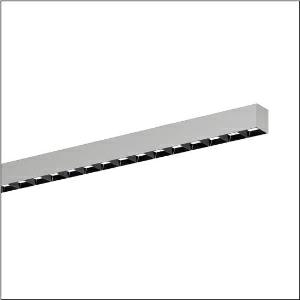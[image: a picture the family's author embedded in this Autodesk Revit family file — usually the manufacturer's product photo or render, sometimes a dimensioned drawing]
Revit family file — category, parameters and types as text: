
# Revit family: silica_r__21_51mx24tctas_d744
name_source: partatom
category: Lighting Fixtures
units: mm (PartAtom-declared; Revit-internal decimal feet)

## family parameters
Cut with Voids When Loaded = No
Host = Face
Light Source = No
Part Type = Normal
Room Calculation Point = No
Round Connector Dimension = Use Diameter
Shared = No

## types (1)
- --- (1 x LED, 8200 lm, 81.1 W, 6500K)
    Apparent Load = 81 VA
    CIE Flux Codes = 74 94 99 100 100
    Color Rendering = 80
    Color Temperature = 6500K
    Default Elevation = 1800 mm
    Description = Silica® 21, office luminaire, primary light control with darklight reflector, of PMMA, black, light emission: direct distribution, primary light characteristic: asymmetric, installation type: surface-mounted, LED, rated luminous flux: 8.200lm, luminous efficacy: 96lm/W, light colour: 8tw, colour temperature: 2700..6500K, control gear: ECG DALI, with terminal, 3+2-pole, max. 2.5mm², mains connection: 220..240V, AC, 50/60Hz, rated input power: 85.2W, luminaire housing, of aluminium, metallic grey (RAL 9006), length: 3.004mm, width: 53mm, height: 53mm, protection rating (complete): IP20, insulation class (complete): insulation class I (protective earthing), certification: CE, permissible operating ambient temperature: 0..+35°C, standard: EN 50419, packaging unit: 1 piece
    Height = 0 mm  [stored 0 ft]
    Lamp = 1 x LED
    Lamp Light Flux = 8200 lm
    Lamp Power = 81.1 W
    Lamp count = 1
    Length = 3004 mm
    Luminous efficacy = 101 lm/W
    Manufacturer = Siteco
    ModVariant = No
    Model = 51MX24TCTAS
    Mounting Place = Ceiling
    Mounting Type = Recessed
    Number of Poles = 1
    OnlyDefault = Yes
    Power Factor = 1
    Product Name = Silica® 21
    Product group = office luminaire | ceiling recessed
    ProductGroupID = 401
    Protection Class = Protection class I
    Protection Degree = IP 20
    RLX_Detail_Level = 1
    RLX_Emergency_Light_Flux = 0 lm
    RLX_Emergency_Type = 0
    RLX_Emergency_Type_DB = No
    RlxData = <blob elided: 61205 chars, md5=0fd7b8c8>
    Socket = socket
    Standby Power = 0 W
    System Light Flux = 8200 lm
    System Power = 81 W
    Type Comments = individual setting
    Type Image = l_1297764.jpg
    URL = http://relux.com
    VarID = @adj_071293
    Voltage = 0 V
    Weight = 0.00 kg
    Width = 53 mm

note: [stored X ft] marks values corroborated as IEEE doubles in the binary element streams (Revit-internal decimal feet)

## geometry (parser evidence)
native form markers: Blend x4, Sweep x13
no freeform markers — native parametric forms only
